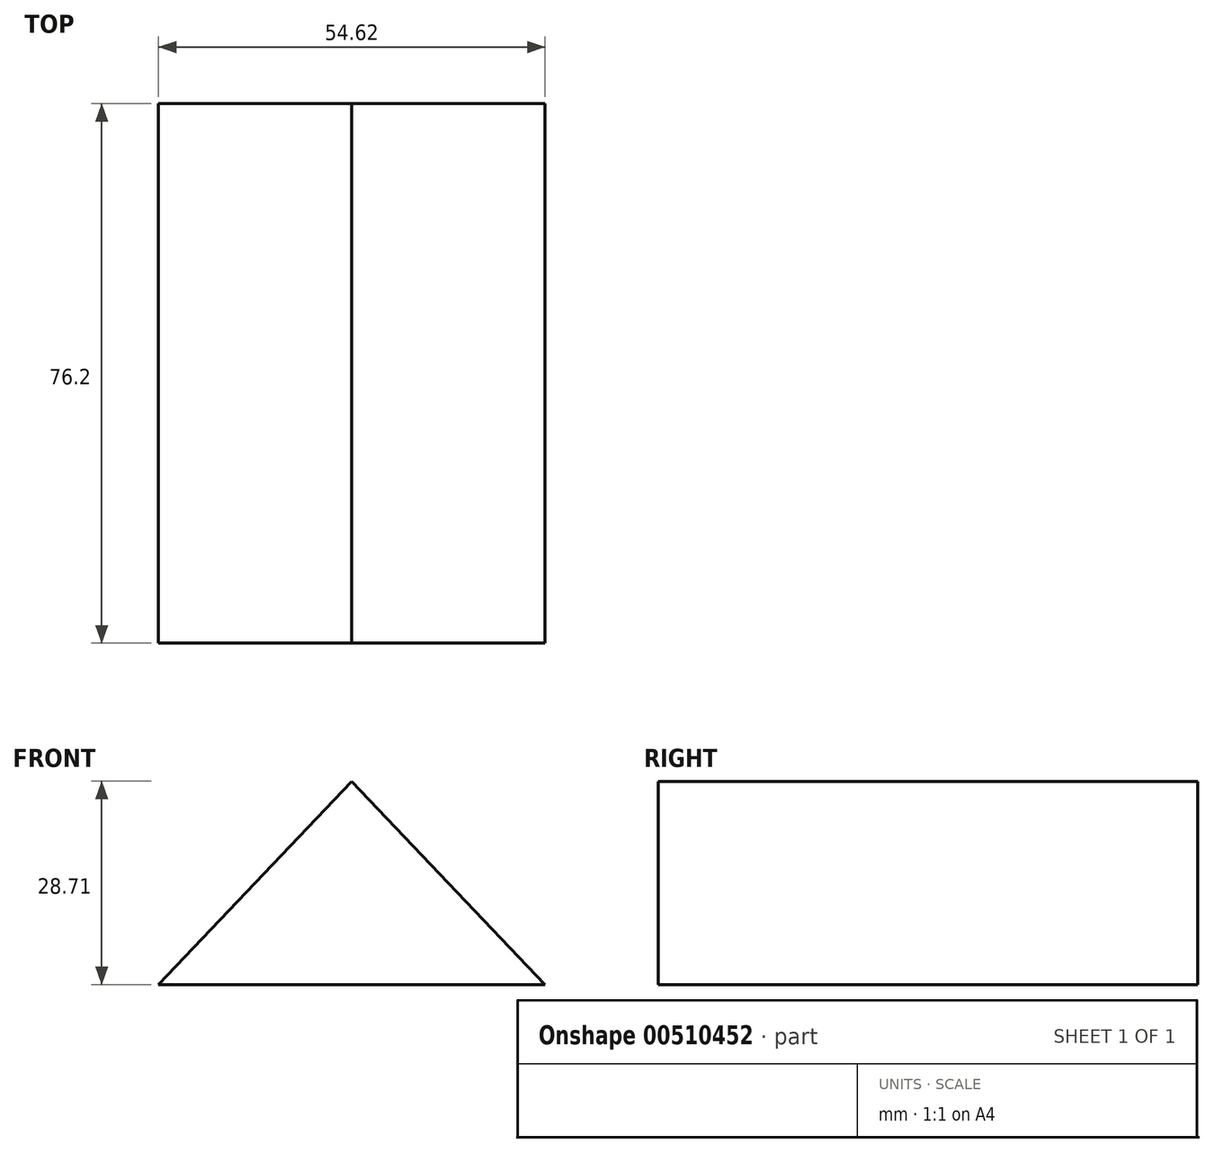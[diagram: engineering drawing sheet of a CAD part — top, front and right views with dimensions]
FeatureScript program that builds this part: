
annotation { "Feature Type Name" : "Feature", "Feature Type Description" : "" }
export const myFeature = defineFeature(function(context is Context, id is Id, definition is map)
    precondition{}
    {
        {
            var Q0;
            Q0=qCreatedBy(makeId("Front.planeOp"),FACE);
            var sketch = newSketch(context, id + "F0", { "sketchPlane" : qUnion([Q0])});
            skLineSegment(sketch, "E0", {"start": v(0, 16.13) * mm, "end": v(-27.3, -12.58) * mm});
            skLineSegment(sketch, "E1", {"start": v(0, 16.13) * mm, "end": v(27.3, -12.58) * mm});
            skLineSegment(sketch, "E2", {"start": v(-27.3, -12.58) * mm, "end": v(27.3, -12.58) * mm});
            skSolve(sketch);
        }
        {
            var Q0;
            Q0=makeQuery(id+"F0.imprint","IMPRINT",FACE,{"disambiguationData":[TD([[makeQuery(id+"F0.imprint","IMPRINT",EDGE,{"derivedFrom":sQuery(id+"F0.wireOp",EDGE,"E0")}),1.0]])]});
            extrude(context, id + "F1", {"entities" : qUnion([Q0]), "depth" : 76.2 * mm});
        }
    });
